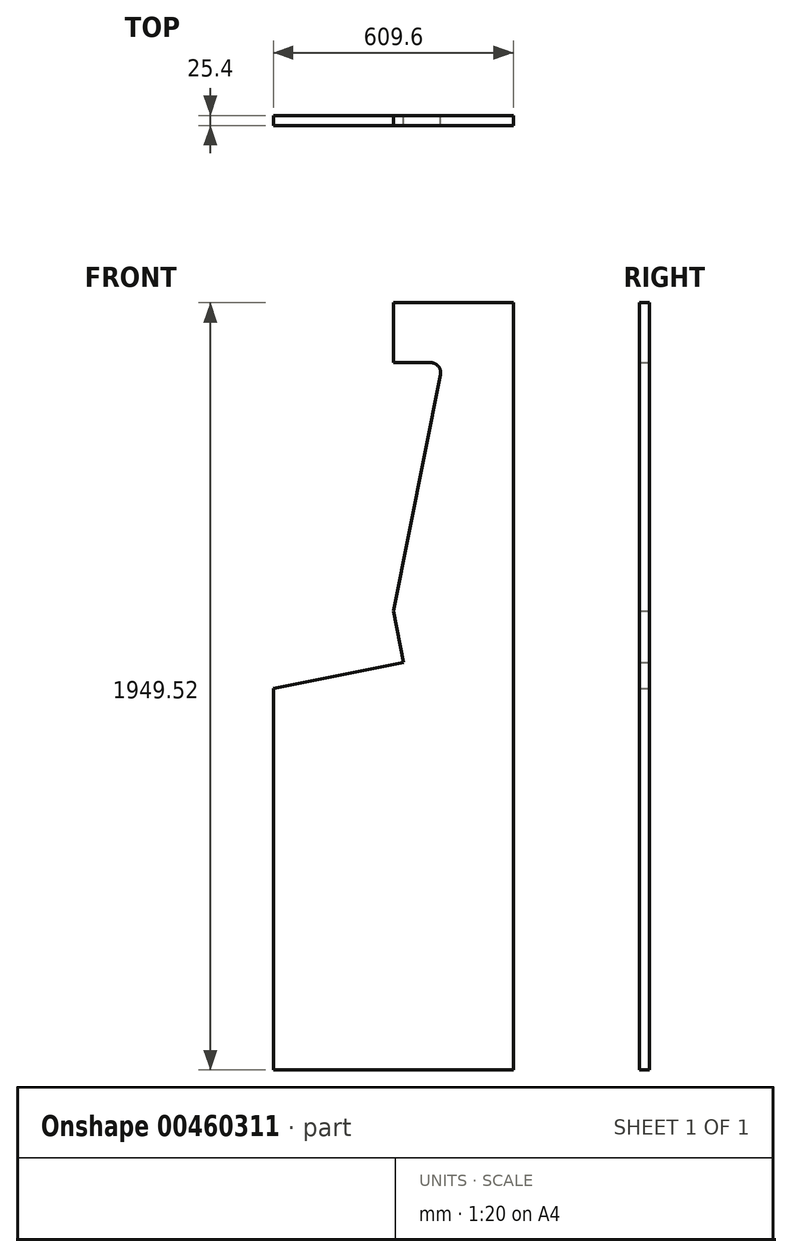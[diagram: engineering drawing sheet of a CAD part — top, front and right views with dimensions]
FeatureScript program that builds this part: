
annotation { "Feature Type Name" : "Feature", "Feature Type Description" : "" }
export const myFeature = defineFeature(function(context is Context, id is Id, definition is map)
    precondition{}
    {
        {
            var Q0;
            Q0=qCreatedBy(makeId("Front.planeOp"),FACE);
            var sketch = newSketch(context, id + "F0", { "sketchPlane" : qUnion([Q0])});
            skLineSegment(sketch, "E0.bottom", {"start": v(0, 958.92) * mm, "end": v(94.6, 958.92) * mm});
            skLineSegment(sketch, "E0.top", {"start": v(-304.8, -838.2) * mm, "end": v(304.8, -838.2) * mm});
            skLineSegment(sketch, "E0.left", {"start": v(-304.8, 131.11) * mm, "end": v(-304.8, -838.2) * mm});
            skLineSegment(sketch, "E0.right", {"start": v(304.8, 1111.32) * mm, "end": v(304.8, -838.2) * mm});
            skLineSegment(sketch, "E1", {"start": v(-304.8, 131.11) * mm, "end": v(26.02, 196.92) * mm});
            skLineSegment(sketch, "E2", {"start": v(-304.8, 267.08) * mm, "end": v(0, 327.7) * mm, "construction": true});
            skLineSegment(sketch, "E3", {"start": v(-498.24, 228.6) * mm, "end": v(-498.24, -838.2) * mm, "construction": true});
            skLineSegment(sketch, "E4", {"start": v(0, 327.7) * mm, "end": v(26.02, 196.92) * mm});
            skPoint(sketch, "E5.orphan", {"position": v(0, 191.74) * mm});
            skLineSegment(sketch, "E6", {"start": v(0, 327.7) * mm, "end": v(119.52, 928.56) * mm});
            skLineSegment(sketch, "E7", {"start": v(0, 958.92) * mm, "end": v(0, 1111.32) * mm});
            skLineSegment(sketch, "E8", {"start": v(0, 1111.32) * mm, "end": v(304.8, 1111.32) * mm});
            skPoint(sketch, "E9.visualSharp", {"position": v(125.56, 958.92) * mm});
            skArc(sketch, "E9.filletArc", {"start": v(119.52, 928.56) * mm, "mid": v(114.24, 949.63) * mm, "end": v(94.6, 958.92) * mm});
            skSolve(sketch);
        }
        {
            var Q0;
            Q0 = qSketchRegion(id + "F0", true);
            extrude(context, id + "F1", {"entities" : qUnion([Q0]), "depth" : 25.4 * mm});
        }
    });
